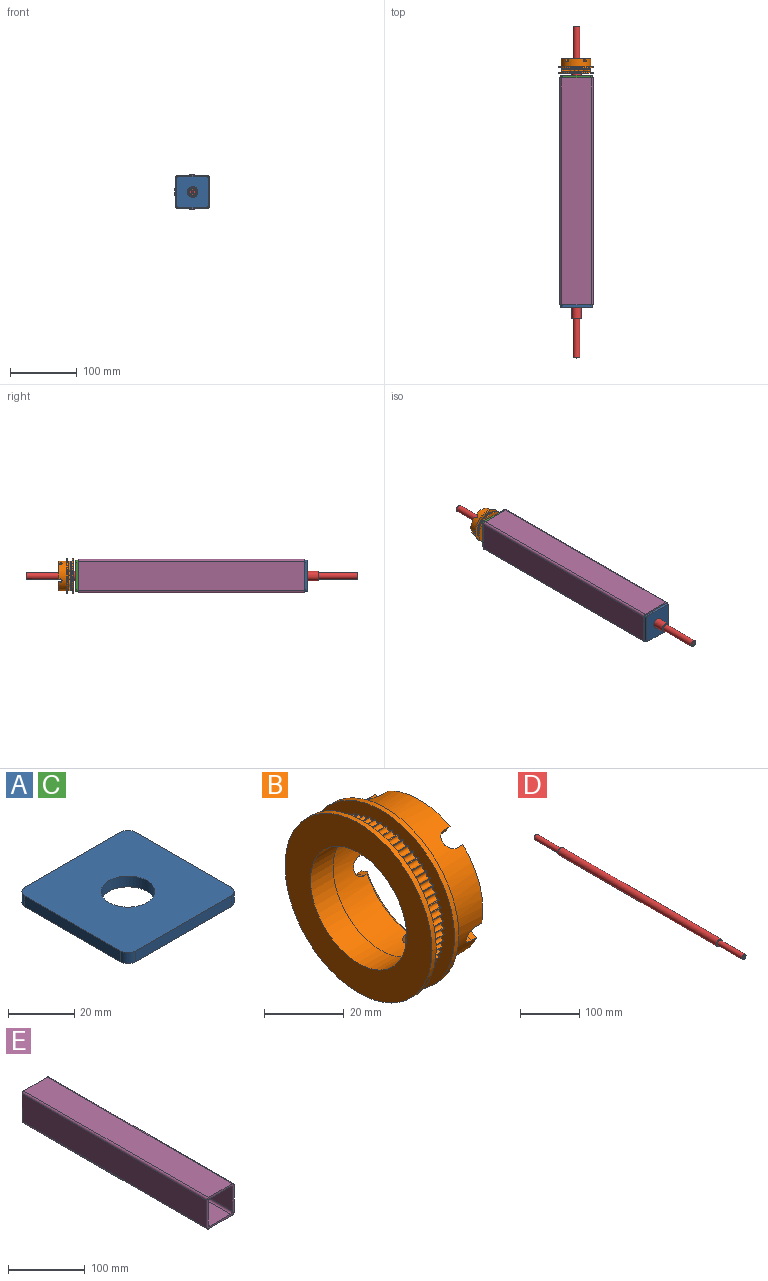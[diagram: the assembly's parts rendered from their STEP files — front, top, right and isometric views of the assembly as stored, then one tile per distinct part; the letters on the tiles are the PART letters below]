
ASSEMBLY  parts=5 mates=3
PART A: 11 faces, bbox 47x47x4 mm
  f0: plane 41x4mm, normal (0,1,0), area 164mm2, adj f5,f6,f7,f10
  f1: plane 41x4mm, normal (-1,0,0), area 164mm2, adj f5,f6,f7,f8
  f2: plane 41x4mm, normal (0,-1,0), area 164mm2, adj f5,f6,f8,f9
  f3: cylinder r=8.12mm len=16.25mm, axis (0,0,-1), area 204.2mm2, adj f5,f6
  f4: plane 41x4mm, normal (1,0,0), area 164mm2, adj f5,f6,f9,f10
  f5: plane 47x47mm, normal (0,0,1), area 1993.9mm2, adj f0,f1,f2,f3,f4,f7,f8,f9
  f6: plane 47x47mm, normal (0,0,-1), area 1993.9mm2, adj f0,f1,f2,f3,f4,f7,f8,f9
  f7: cylinder r=3mm len=4mm, axis (0,0,1), area 18.8mm2, adj f0,f1,f5,f6
  f8: cylinder r=3mm len=4mm, axis (0,0,-1), area 18.8mm2, adj f1,f2,f5,f6
  f9: cylinder r=3mm len=4mm, axis (0,0,1), area 18.8mm2, adj f2,f4,f5,f6
  f10: cylinder r=3mm len=4mm, axis (0,0,-1), area 18.8mm2, adj f0,f4,f5,f6
PART B: 175 faces, bbox 21.5x52x52 mm
  f0: plane 20.74x8.41mm, normal (1,0,0), area 45.5mm2, adj f1,f154,f170,f174
  f1: cone r=19.38mm half-angle=45deg, axis (1,0,0), area 27.5mm2, adj f0,f158,f170,f174
  f2: plane 21.8x4.55mm, normal (1,0,0), area 45.5mm2, adj f3,f154,f167,f171
  f3: cone r=19.38mm half-angle=45deg, axis (1,0,0), area 27.5mm2, adj f2,f158,f167,f171
  f4: plane 20.74x8.41mm, normal (1,0,0), area 45.5mm2, adj f5,f154,f164,f168
  f5: cone r=19.38mm half-angle=45deg, axis (1,0,0), area 27.5mm2, adj f4,f158,f164,f168
  f6: plane 17.64x13.48mm, normal (1,0,0), area 45.5mm2, adj f7,f154,f161,f165
  f7: cone r=19.38mm half-angle=45deg, axis (1,0,0), area 27.5mm2, adj f6,f158,f161,f165
  f8: cylinder r=22.28mm len=6.5mm, axis (-1,0,0), area 1.3mm2, adj f78,f147,f148,f151
  f9: cylinder r=22.28mm len=6.5mm, axis (-1,0,0), area 1.3mm2, adj f146,f147,f148,f151
  f10: cylinder r=22.28mm len=6.5mm, axis (-1,0,0), area 1.3mm2, adj f145,f146,f148,f151
  f11: cylinder r=22.28mm len=6.5mm, axis (-1,0,0), area 1.3mm2, adj f144,f145,f148,f151
  f12: cylinder r=22.28mm len=6.5mm, axis (-1,0,0), area 1.3mm2, adj f143,f144,f148,f151
  f13: cylinder r=22.28mm len=6.5mm, axis (-1,0,0), area 1.3mm2, adj f142,f143,f148,f151
  f14: cylinder r=22.28mm len=6.5mm, axis (-1,0,0), area 1.3mm2, adj f141,f142,f148,f151
  f15: cylinder r=22.28mm len=6.5mm, axis (-1,0,0), area 1.3mm2, adj f140,f141,f148,f151
  f16: cylinder r=22.28mm len=6.5mm, axis (-1,0,0), area 1.3mm2, adj f139,f140,f148,f151
  f17: cylinder r=22.28mm len=6.5mm, axis (-1,0,0), area 1.3mm2, adj f138,f139,f148,f151
  f18: cylinder r=22.28mm len=6.5mm, axis (-1,0,0), area 1.3mm2, adj f137,f138,f148,f151
  f19: cylinder r=22.28mm len=6.5mm, axis (-1,0,0), area 1.3mm2, adj f136,f137,f148,f151
  f20: cylinder r=22.28mm len=6.5mm, axis (-1,0,0), area 1.3mm2, adj f135,f136,f148,f151
  f21: cylinder r=22.28mm len=6.5mm, axis (-1,0,0), area 1.3mm2, adj f134,f135,f148,f151
  f22: cylinder r=22.28mm len=6.5mm, axis (-1,0,0), area 1.3mm2, adj f133,f134,f148,f151
  f23: cylinder r=22.28mm len=6.5mm, axis (-1,0,0), area 1.3mm2, adj f132,f133,f148,f151
  f24: cylinder r=22.28mm len=6.5mm, axis (-1,0,0), area 1.3mm2, adj f131,f132,f148,f151
  f25: cylinder r=22.28mm len=6.5mm, axis (-1,0,0), area 1.3mm2, adj f130,f131,f148,f151
  f26: cylinder r=22.28mm len=6.5mm, axis (-1,0,0), area 1.3mm2, adj f129,f130,f148,f151
  f27: cylinder r=22.28mm len=6.5mm, axis (-1,0,0), area 1.3mm2, adj f128,f129,f148,f151
  f28: cylinder r=22.28mm len=6.5mm, axis (-1,0,0), area 1.3mm2, adj f127,f128,f148,f151
  f29: cylinder r=22.28mm len=6.5mm, axis (-1,0,0), area 1.3mm2, adj f126,f127,f148,f151
  f30: cylinder r=22.28mm len=6.5mm, axis (-1,0,0), area 1.3mm2, adj f125,f126,f148,f151
  f31: cylinder r=22.28mm len=6.5mm, axis (-1,0,0), area 1.3mm2, adj f124,f125,f148,f151
  f32: cylinder r=22.28mm len=6.5mm, axis (-1,0,0), area 1.3mm2, adj f123,f124,f148,f151
  f33: cylinder r=22.28mm len=6.5mm, axis (-1,0,0), area 1.3mm2, adj f122,f123,f148,f151
  f34: cylinder r=22.28mm len=6.5mm, axis (-1,0,0), area 1.3mm2, adj f121,f122,f148,f151
  f35: cylinder r=22.28mm len=6.5mm, axis (-1,0,0), area 1.3mm2, adj f120,f121,f148,f151
  f36: cylinder r=22.28mm len=6.5mm, axis (-1,0,0), area 1.3mm2, adj f119,f120,f148,f151
  f37: cylinder r=22.28mm len=6.5mm, axis (-1,0,0), area 1.3mm2, adj f118,f119,f148,f151
  f38: cylinder r=22.28mm len=6.5mm, axis (-1,0,0), area 1.3mm2, adj f117,f118,f148,f151
  f39: cylinder r=22.28mm len=6.5mm, axis (-1,0,0), area 1.3mm2, adj f116,f117,f148,f151
  f40: cylinder r=22.28mm len=6.5mm, axis (-1,0,0), area 1.3mm2, adj f115,f116,f148,f151
  f41: cylinder r=22.28mm len=6.5mm, axis (-1,0,0), area 1.3mm2, adj f114,f115,f148,f151
  f42: cylinder r=22.28mm len=6.5mm, axis (-1,0,0), area 1.3mm2, adj f113,f114,f148,f151
  f43: cylinder r=22.28mm len=6.5mm, axis (-1,0,0), area 1.3mm2, adj f112,f113,f148,f151
  f44: cylinder r=22.28mm len=6.5mm, axis (-1,0,0), area 1.3mm2, adj f111,f112,f148,f151
  f45: cylinder r=22.28mm len=6.5mm, axis (-1,0,0), area 1.3mm2, adj f110,f111,f148,f151
  f46: cylinder r=22.28mm len=6.5mm, axis (-1,0,0), area 1.3mm2, adj f109,f110,f148,f151
  f47: cylinder r=22.28mm len=6.5mm, axis (-1,0,0), area 1.3mm2, adj f108,f109,f148,f151
  f48: cylinder r=22.28mm len=6.5mm, axis (-1,0,0), area 1.3mm2, adj f107,f108,f148,f151
  f49: cylinder r=22.28mm len=6.5mm, axis (-1,0,0), area 1.3mm2, adj f106,f107,f148,f151
  f50: cylinder r=22.28mm len=6.5mm, axis (-1,0,0), area 1.3mm2, adj f105,f106,f148,f151
  f51: cylinder r=22.28mm len=6.5mm, axis (-1,0,0), area 1.3mm2, adj f104,f105,f148,f151
  f52: cylinder r=22.28mm len=6.5mm, axis (-1,0,0), area 1.3mm2, adj f103,f104,f148,f151
  f53: cylinder r=22.28mm len=6.5mm, axis (-1,0,0), area 1.3mm2, adj f102,f103,f148,f151
  f54: cylinder r=22.28mm len=6.5mm, axis (-1,0,0), area 1.3mm2, adj f101,f102,f148,f151
  f55: cylinder r=22.28mm len=6.5mm, axis (-1,0,0), area 1.3mm2, adj f100,f101,f148,f151
  f56: cylinder r=22.28mm len=6.5mm, axis (-1,0,0), area 1.3mm2, adj f99,f100,f148,f151
  f57: cylinder r=22.28mm len=6.5mm, axis (-1,0,0), area 1.3mm2, adj f98,f99,f148,f151
  f58: cylinder r=22.28mm len=6.5mm, axis (-1,0,0), area 1.3mm2, adj f97,f98,f148,f151
  f59: cylinder r=22.28mm len=6.5mm, axis (-1,0,0), area 1.3mm2, adj f96,f97,f148,f151
  f60: cylinder r=22.28mm len=6.5mm, axis (-1,0,0), area 1.3mm2, adj f95,f96,f148,f151
  f61: cylinder r=22.28mm len=6.5mm, axis (-1,0,0), area 1.3mm2, adj f94,f95,f148,f151
  f62: cylinder r=22.28mm len=6.5mm, axis (-1,0,0), area 1.3mm2, adj f93,f94,f148,f151
  f63: cylinder r=22.28mm len=6.5mm, axis (-1,0,0), area 1.3mm2, adj f92,f93,f148,f151
  f64: cylinder r=22.28mm len=6.5mm, axis (-1,0,0), area 1.3mm2, adj f91,f92,f148,f151
  f65: cylinder r=22.28mm len=6.5mm, axis (-1,0,0), area 1.3mm2, adj f90,f91,f148,f151
  f66: cylinder r=22.28mm len=6.5mm, axis (-1,0,0), area 1.3mm2, adj f89,f90,f148,f151
  f67: cylinder r=22.28mm len=6.5mm, axis (-1,0,0), area 1.3mm2, adj f88,f89,f148,f151
  f68: cylinder r=22.28mm len=6.5mm, axis (-1,0,0), area 1.3mm2, adj f87,f88,f148,f151
  f69: cylinder r=22.28mm len=6.5mm, axis (-1,0,0), area 1.3mm2, adj f86,f87,f148,f151
  f70: cylinder r=22.28mm len=6.5mm, axis (-1,0,0), area 1.3mm2, adj f85,f86,f148,f151
  f71: cylinder r=22.28mm len=6.5mm, axis (-1,0,0), area 1.3mm2, adj f84,f85,f148,f151
  f72: cylinder r=22.28mm len=6.5mm, axis (-1,0,0), area 1.3mm2, adj f83,f84,f148,f151
  f73: cylinder r=22.28mm len=6.5mm, axis (-1,0,0), area 1.3mm2, adj f82,f83,f148,f151
  f74: cylinder r=22.28mm len=6.5mm, axis (-1,0,0), area 1.3mm2, adj f81,f82,f148,f151
  f75: cylinder r=22.28mm len=6.5mm, axis (-1,0,0), area 1.3mm2, adj f80,f81,f148,f151
  f76: cylinder r=22.28mm len=6.5mm, axis (-1,0,0), area 1.3mm2, adj f79,f80,f148,f151
  f77: cylinder r=22.28mm len=6.5mm, axis (-1,0,0), area 1.3mm2, adj f78,f79,f148,f151
  f78: cylinder r=0.9mm len=6.5mm, axis (1,0,0), area 18.1mm2, adj f8,f77,f148,f151
  f79: cylinder r=0.9mm len=6.5mm, axis (1,0,0), area 18.1mm2, adj f76,f77,f148,f151
  f80: cylinder r=0.9mm len=6.5mm, axis (1,0,0), area 18.1mm2, adj f75,f76,f148,f151
  f81: cylinder r=0.9mm len=6.5mm, axis (1,0,0), area 18.1mm2, adj f74,f75,f148,f151
  f82: cylinder r=0.9mm len=6.5mm, axis (1,0,0), area 18.1mm2, adj f73,f74,f148,f151
  f83: cylinder r=0.9mm len=6.5mm, axis (1,0,0), area 18.1mm2, adj f72,f73,f148,f151
  f84: cylinder r=0.9mm len=6.5mm, axis (1,0,0), area 18.1mm2, adj f71,f72,f148,f151
  f85: cylinder r=0.9mm len=6.5mm, axis (1,0,0), area 18.1mm2, adj f70,f71,f148,f151
  f86: cylinder r=0.9mm len=6.5mm, axis (1,0,0), area 18.1mm2, adj f69,f70,f148,f151
  f87: cylinder r=0.9mm len=6.5mm, axis (1,0,0), area 18.1mm2, adj f68,f69,f148,f151
  f88: cylinder r=0.9mm len=6.5mm, axis (1,0,0), area 18.1mm2, adj f67,f68,f148,f151
  f89: cylinder r=0.9mm len=6.5mm, axis (1,0,0), area 18.1mm2, adj f66,f67,f148,f151
  f90: cylinder r=0.9mm len=6.5mm, axis (1,0,0), area 18.1mm2, adj f65,f66,f148,f151
  f91: cylinder r=0.9mm len=6.5mm, axis (1,0,0), area 18.1mm2, adj f64,f65,f148,f151
  f92: cylinder r=0.9mm len=6.5mm, axis (1,0,0), area 18.1mm2, adj f63,f64,f148,f151
  f93: cylinder r=0.9mm len=6.5mm, axis (1,0,0), area 18.1mm2, adj f62,f63,f148,f151
  f94: cylinder r=0.9mm len=6.5mm, axis (1,0,0), area 18.1mm2, adj f61,f62,f148,f151
  f95: cylinder r=0.9mm len=6.5mm, axis (1,0,0), area 18.1mm2, adj f60,f61,f148,f151
  f96: cylinder r=0.9mm len=6.5mm, axis (1,0,0), area 18.1mm2, adj f59,f60,f148,f151
  f97: cylinder r=0.9mm len=6.5mm, axis (1,0,0), area 18.1mm2, adj f58,f59,f148,f151
  f98: cylinder r=0.9mm len=6.5mm, axis (1,0,0), area 18.1mm2, adj f57,f58,f148,f151
  f99: cylinder r=0.9mm len=6.5mm, axis (1,0,0), area 18.1mm2, adj f56,f57,f148,f151
  f100: cylinder r=0.9mm len=6.5mm, axis (1,0,0), area 18.1mm2, adj f55,f56,f148,f151
  f101: cylinder r=0.9mm len=6.5mm, axis (1,0,0), area 18.1mm2, adj f54,f55,f148,f151
  f102: cylinder r=0.9mm len=6.5mm, axis (1,0,0), area 18.1mm2, adj f53,f54,f148,f151
  f103: cylinder r=0.9mm len=6.5mm, axis (1,0,0), area 18.1mm2, adj f52,f53,f148,f151
  f104: cylinder r=0.9mm len=6.5mm, axis (1,0,0), area 18.1mm2, adj f51,f52,f148,f151
  f105: cylinder r=0.9mm len=6.5mm, axis (1,0,0), area 18.1mm2, adj f50,f51,f148,f151
  f106: cylinder r=0.9mm len=6.5mm, axis (1,0,0), area 18.1mm2, adj f49,f50,f148,f151
  f107: cylinder r=0.9mm len=6.5mm, axis (1,0,0), area 18.1mm2, adj f48,f49,f148,f151
  f108: cylinder r=0.9mm len=6.5mm, axis (1,0,0), area 18.1mm2, adj f47,f48,f148,f151
  f109: cylinder r=0.9mm len=6.5mm, axis (1,0,0), area 18.1mm2, adj f46,f47,f148,f151
  f110: cylinder r=0.9mm len=6.5mm, axis (1,0,0), area 18.1mm2, adj f45,f46,f148,f151
  f111: cylinder r=0.9mm len=6.5mm, axis (1,0,0), area 18.1mm2, adj f44,f45,f148,f151
  f112: cylinder r=0.9mm len=6.5mm, axis (1,0,0), area 18.1mm2, adj f43,f44,f148,f151
  f113: cylinder r=0.9mm len=6.5mm, axis (1,0,0), area 18.1mm2, adj f42,f43,f148,f151
  f114: cylinder r=0.9mm len=6.5mm, axis (1,0,0), area 18.1mm2, adj f41,f42,f148,f151
  f115: cylinder r=0.9mm len=6.5mm, axis (1,0,0), area 18.1mm2, adj f40,f41,f148,f151
  f116: cylinder r=0.9mm len=6.5mm, axis (1,0,0), area 18.1mm2, adj f39,f40,f148,f151
  f117: cylinder r=0.9mm len=6.5mm, axis (1,0,0), area 18.1mm2, adj f38,f39,f148,f151
  f118: cylinder r=0.9mm len=6.5mm, axis (1,0,0), area 18.1mm2, adj f37,f38,f148,f151
  f119: cylinder r=0.9mm len=6.5mm, axis (1,0,0), area 18.1mm2, adj f36,f37,f148,f151
  f120: cylinder r=0.9mm len=6.5mm, axis (1,0,0), area 18.1mm2, adj f35,f36,f148,f151
  f121: cylinder r=0.9mm len=6.5mm, axis (1,0,0), area 18.1mm2, adj f34,f35,f148,f151
  f122: cylinder r=0.9mm len=6.5mm, axis (1,0,0), area 18.1mm2, adj f33,f34,f148,f151
  f123: cylinder r=0.9mm len=6.5mm, axis (1,0,0), area 18.1mm2, adj f32,f33,f148,f151
  f124: cylinder r=0.9mm len=6.5mm, axis (1,0,0), area 18.1mm2, adj f31,f32,f148,f151
  f125: cylinder r=0.9mm len=6.5mm, axis (1,0,0), area 18.1mm2, adj f30,f31,f148,f151
  f126: cylinder r=0.9mm len=6.5mm, axis (1,0,0), area 18.1mm2, adj f29,f30,f148,f151
  f127: cylinder r=0.9mm len=6.5mm, axis (1,0,0), area 18.1mm2, adj f28,f29,f148,f151
  f128: cylinder r=0.9mm len=6.5mm, axis (1,0,0), area 18.1mm2, adj f27,f28,f148,f151
  f129: cylinder r=0.9mm len=6.5mm, axis (1,0,0), area 18.1mm2, adj f26,f27,f148,f151
  f130: cylinder r=0.9mm len=6.5mm, axis (1,0,0), area 18.1mm2, adj f25,f26,f148,f151
  f131: cylinder r=0.9mm len=6.5mm, axis (1,0,0), area 18.1mm2, adj f24,f25,f148,f151
  f132: cylinder r=0.9mm len=6.5mm, axis (1,0,0), area 18.1mm2, adj f23,f24,f148,f151
  f133: cylinder r=0.9mm len=6.5mm, axis (1,0,0), area 18.1mm2, adj f22,f23,f148,f151
  f134: cylinder r=0.9mm len=6.5mm, axis (1,0,0), area 18.1mm2, adj f21,f22,f148,f151
  f135: cylinder r=0.9mm len=6.5mm, axis (1,0,0), area 18.1mm2, adj f20,f21,f148,f151
  f136: cylinder r=0.9mm len=6.5mm, axis (1,0,0), area 18.1mm2, adj f19,f20,f148,f151
  f137: cylinder r=0.9mm len=6.5mm, axis (1,0,0), area 18.1mm2, adj f18,f19,f148,f151
  f138: cylinder r=0.9mm len=6.5mm, axis (1,0,0), area 18.1mm2, adj f17,f18,f148,f151
  f139: cylinder r=0.9mm len=6.5mm, axis (1,0,0), area 18.1mm2, adj f16,f17,f148,f151
  f140: cylinder r=0.9mm len=6.5mm, axis (1,0,0), area 18.1mm2, adj f15,f16,f148,f151
  f141: cylinder r=0.9mm len=6.5mm, axis (1,0,0), area 18.1mm2, adj f14,f15,f148,f151
  f142: cylinder r=0.9mm len=6.5mm, axis (1,0,0), area 18.1mm2, adj f13,f14,f148,f151
  f143: cylinder r=0.9mm len=6.5mm, axis (1,0,0), area 18.1mm2, adj f12,f13,f148,f151
  f144: cylinder r=0.9mm len=6.5mm, axis (1,0,0), area 18.1mm2, adj f11,f12,f148,f151
  f145: cylinder r=0.9mm len=6.5mm, axis (1,0,0), area 18.1mm2, adj f10,f11,f148,f151
  f146: cylinder r=0.9mm len=6.5mm, axis (1,0,0), area 18.1mm2, adj f9,f10,f148,f151
  f147: cylinder r=0.9mm len=6.5mm, axis (1,0,0), area 18.1mm2, adj f8,f9,f148,f151
  f148: plane 52x52mm, normal (-1,0,0), area 652.3mm2, adj f8,f9,f10,f11,f12,f13,f14,f15
  f149: cylinder r=26mm len=52mm, axis (-1,0,0), area 245mm2, adj f148,f150
  f150: plane 52x52mm, normal (1,0,0), area 533.3mm2, adj f149,f154
  f151: plane 52x52mm, normal (1,0,0), area 652.3mm2, adj f8,f9,f10,f11,f12,f13,f14,f15
  f152: cylinder r=26mm len=52mm, axis (1,0,0), area 245mm2, adj f151,f153
  f153: plane 52x52mm, normal (-1,0,0), area 1215.8mm2, adj f152,f156
  f154: cylinder r=22.5mm len=45mm, axis (-1,0,0), area 1581.9mm2, adj f0,f2,f4,f6,f150,f155,f160,f161
  f155: plane 17.64x13.48mm, normal (1,0,0), area 45.5mm2, adj f154,f159,f162,f173
  f156: cylinder r=17mm len=34mm, axis (-1,0,0), area 854.5mm2, adj f153,f157
  f157: plane 38.75x38.75mm, normal (1,0,0), area 271.4mm2, adj f156,f158
  f158: cylinder r=19.38mm len=38.75mm, axis (1,0,0), area 1434.6mm2, adj f1,f3,f5,f7,f157,f159,f160,f161
  f159: cone r=19.38mm half-angle=45deg, axis (1,0,0), area 27.5mm2, adj f155,f158,f162,f173
  f160: cylinder r=2.75mm len=5.5mm, axis (0,0,1), area 26.4mm2, adj f154,f158,f161,f162
  f161: plane 3.16x2mm, normal (0,-1,0), area 5.8mm2, adj f6,f7,f154,f158,f160
  f162: plane 3.16x2mm, normal (0,1,0), area 5.8mm2, adj f154,f155,f158,f159,f160
  f163: cylinder r=2.75mm len=6.21mm, axis (0,-0.95,0.31), area 26.4mm2, adj f154,f158,f164,f165
  f164: plane 3x2mm, normal (0,-0.31,-0.95), area 5.8mm2, adj f4,f5,f154,f158,f163
  f165: plane 3x2mm, normal (0,0.31,0.95), area 5.8mm2, adj f6,f7,f154,f158,f163
  f166: cylinder r=2.75mm len=6.3mm, axis (0,-0.59,-0.81), area 26.4mm2, adj f154,f158,f167,f168
  f167: plane 2.55x2mm, normal (0,0.81,-0.59), area 5.8mm2, adj f2,f3,f154,f158,f166
  f168: plane 2.55x2mm, normal (0,-0.81,0.59), area 5.8mm2, adj f4,f5,f154,f158,f166
  f169: cylinder r=2.75mm len=6.3mm, axis (0,0.59,-0.81), area 26.4mm2, adj f154,f158,f170,f171
  f170: plane 2.55x2mm, normal (0,0.81,0.59), area 5.8mm2, adj f0,f1,f154,f158,f169
  f171: plane 2.55x2mm, normal (0,-0.81,-0.59), area 5.8mm2, adj f2,f3,f154,f158,f169
  f172: cylinder r=2.75mm len=6.21mm, axis (0,0.95,0.31), area 26.4mm2, adj f154,f158,f173,f174
  f173: plane 3x2mm, normal (0,-0.31,0.95), area 5.8mm2, adj f154,f155,f158,f159,f172
  f174: plane 3x2mm, normal (0,0.31,-0.95), area 5.8mm2, adj f0,f1,f154,f158,f172
PART C: same geometry as A
PART D: 15 faces, bbox 14x498x14 mm
  f0: cylinder r=7mm len=379.2mm, axis (0,1,0), area 16678.1mm2, adj f7,f8
  f1: cylinder r=5mm len=58.6mm, axis (0,-1,0), area 1841mm2, adj f2,f9
  f2: plane 13.2x13.2mm, normal (0,-1,0), area 58.3mm2, adj f1,f7
  f3: plane 9.2x9.2mm, normal (0,-1,0), area 52.6mm2, adj f9,f12
  f4: cylinder r=5mm len=58.6mm, axis (0,1,0), area 1841mm2, adj f5,f10
  f5: plane 13.2x13.2mm, normal (0,1,0), area 58.3mm2, adj f4,f8
  f6: plane 9.2x9.2mm, normal (0,1,0), area 52.6mm2, adj f10,f14
  f7: cone r=6.6mm half-angle=45deg, axis (0,1,0), area 24.2mm2, adj f0,f2
  f8: cone r=7mm half-angle=45deg, axis (0,-1,0), area 24.2mm2, adj f0,f5
  f9: cone r=4.6mm half-angle=45deg, axis (0,1,0), area 17.1mm2, adj f1,f3
  f10: cone r=4.6mm half-angle=45deg, axis (0,-1,0), area 17.1mm2, adj f4,f6
  f11: cone r=0mm half-angle=59deg, axis (0,-1,0), area 16.2mm2, adj f12
  f12: cylinder r=2.1mm len=14.4mm, axis (0,-1,0), area 190mm2, adj f3,f11
  f13: cone r=0mm half-angle=59deg, axis (0,1,0), area 16.2mm2, adj f14
  f14: cylinder r=2.1mm len=14.4mm, axis (0,1,0), area 190mm2, adj f6,f13
PART E: 18 faces, bbox 50x340x50 mm
  f0: plane 340x38mm, normal (0,0,-1), area 12920mm2, adj f8,f9,f10,f13
  f1: plane 340x38mm, normal (-1,0,0), area 12920mm2, adj f8,f9,f10,f11
  f2: plane 340x38mm, normal (0,0,1), area 12920mm2, adj f8,f9,f11,f12
  f3: plane 340x44mm, normal (1,0,0), area 14960mm2, adj f8,f9,f14,f17
  f4: plane 340x44mm, normal (0,0,1), area 14960mm2, adj f8,f9,f14,f15
  f5: plane 340x44mm, normal (-1,0,0), area 14960mm2, adj f8,f9,f15,f16
  f6: plane 340x44mm, normal (0,0,-1), area 14960mm2, adj f8,f9,f16,f17
  f7: plane 340x38mm, normal (1,0,0), area 12920mm2, adj f8,f9,f12,f13
  f8: plane 50x50mm, normal (0,-1,0), area 564mm2, adj f0,f1,f2,f3,f4,f5,f6,f7
  f9: plane 50x50mm, normal (0,1,0), area 564mm2, adj f0,f1,f2,f3,f4,f5,f6,f7
  f10: cylinder r=3mm len=340mm, axis (0,1,0), area 1602.2mm2, adj f0,f1,f8,f9
  f11: cylinder r=3mm len=340mm, axis (0,-1,0), area 1602.2mm2, adj f1,f2,f8,f9
  f12: cylinder r=3mm len=340mm, axis (0,1,0), area 1602.2mm2, adj f2,f7,f8,f9
  f13: cylinder r=3mm len=340mm, axis (0,-1,0), area 1602.2mm2, adj f0,f7,f8,f9
  f14: cylinder r=3mm len=340mm, axis (0,-1,0), area 1602.2mm2, adj f3,f4,f8,f9
  f15: cylinder r=3mm len=340mm, axis (0,1,0), area 1602.2mm2, adj f4,f5,f8,f9
  f16: cylinder r=3mm len=340mm, axis (0,-1,0), area 1602.2mm2, adj f5,f6,f8,f9
  f17: cylinder r=3mm len=340mm, axis (0,1,0), area 1602.2mm2, adj f3,f6,f8,f9
PLACE A rot(axis=(-1,0,0),90deg) t=(0,-278,0)mm
PLACE B rot(axis=(0,0,1),90deg) t=(-0.75,74.75,0)mm
PLACE C rot(axis=(-1,0,0),90deg) t=(0,66,0)mm
PLACE D t=(0,144,0)mm
PLACE E t=(0,66,0)mm
MATE cylindrical D.f0 <-> A.f3  axis (0,1,0) through (0,-105,0)mm
MATE planar A.f3 <-> E.f8  axis (0,1,0) through (0,-274,0)mm
MATE planar C.f3 <-> E.f9  axis (0,-1,0) through (0,66,0)mm
